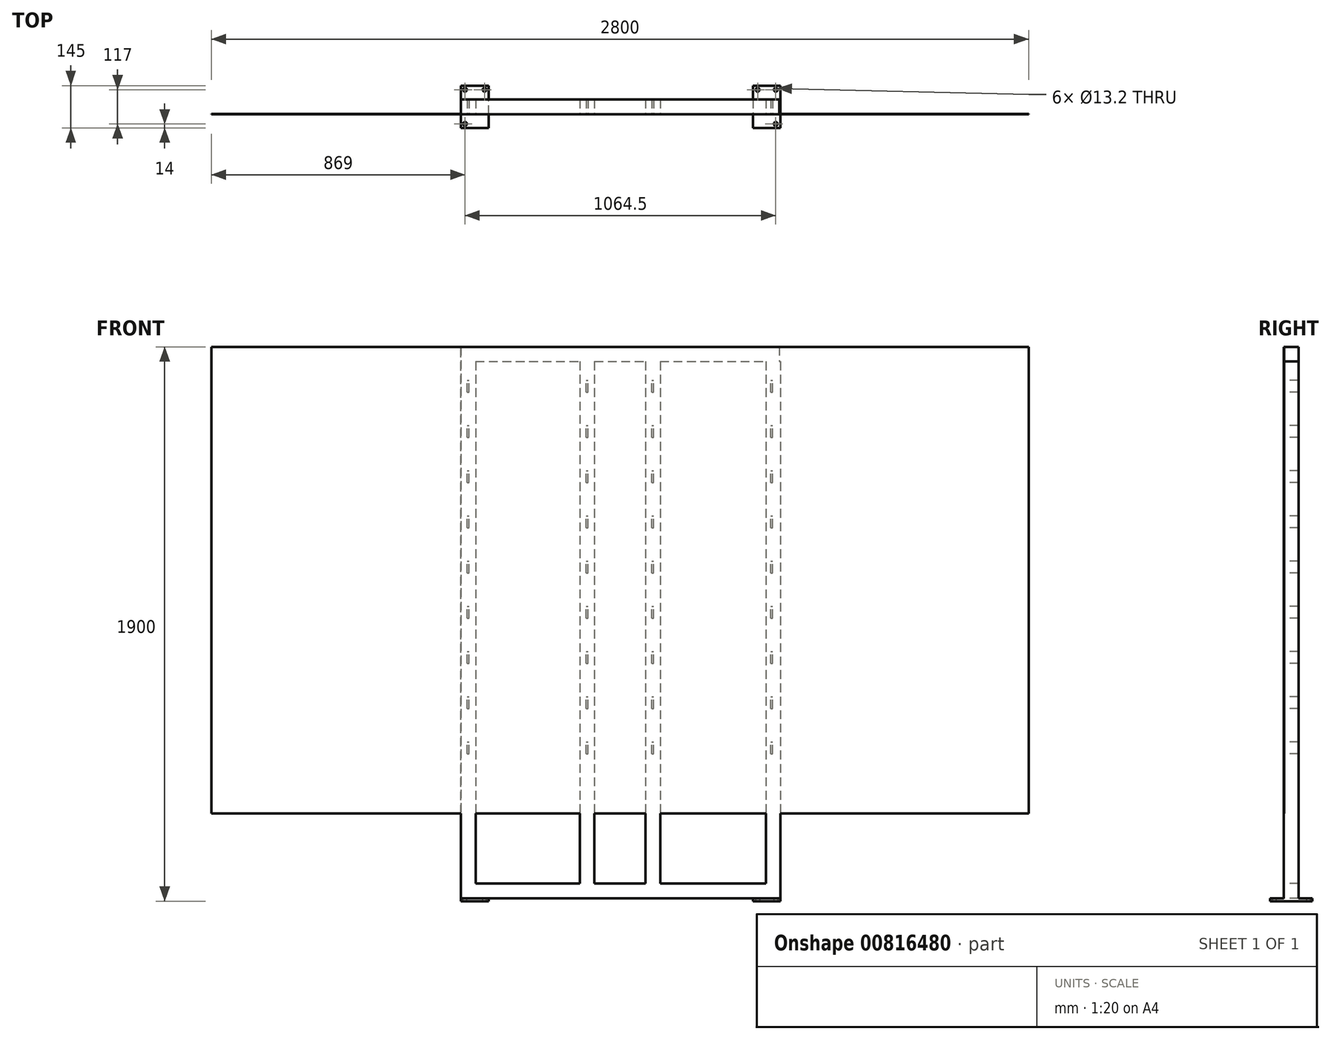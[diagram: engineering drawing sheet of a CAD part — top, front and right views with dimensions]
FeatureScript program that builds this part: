
annotation { "Feature Type Name" : "Feature", "Feature Type Description" : "" }
export const myFeature = defineFeature(function(context is Context, id is Id, definition is map)
    precondition{}
    {
        {
            var Q0;
            Q0=qCreatedBy(makeId("Top.planeOp"),FACE);
            var sketch = newSketch(context, id + "F0", { "sketchPlane" : qUnion([Q0])});
            skLineSegment(sketch, "E0.bottom", {"start": v(47.5, 72.5) * mm, "end": v(-47.5, 72.5) * mm});
            skLineSegment(sketch, "E0.top", {"start": v(47.5, -72.5) * mm, "end": v(-47.5, -72.5) * mm});
            skLineSegment(sketch, "E0.left", {"start": v(47.5, 72.5) * mm, "end": v(47.5, -72.5) * mm});
            skLineSegment(sketch, "E0.right", {"start": v(-47.5, 72.5) * mm, "end": v(-47.5, -72.5) * mm});
            skPoint(sketch, "E0.middle", {"position": v(0, 0) * mm});
            skSolve(sketch);
        }
        {
            var Q0;
            Q0=makeQuery(id+"F0.imprint","IMPRINT",FACE,{"disambiguationData":[TD([[makeQuery(id+"F0.imprint","IMPRINT",EDGE,{"derivedFrom":sQuery(id+"F0.wireOp",EDGE,"E0.bottom")}),1.0]])]});
            extrude(context, id + "F1", {"entities" : qUnion([Q0]), "depth" : 10 * mm, "offsetDistance" : 25 * mm});
        }
        {
            var Q0;
            Q0=qCreatedBy(makeId("Top.planeOp"),FACE);
            var sketch = newSketch(context, id + "F2", { "sketchPlane" : qUnion([Q0])});
            skPoint(sketch, "E1", {"position": v(31, 58.5) * mm});
            skPoint(sketch, "E2", {"position": v(31, -58.5) * mm});
            skPoint(sketch, "E3", {"position": v(-31, 58.5) * mm});
            skSolve(sketch);
        }
        {
            var Q0;
            Q0=sQuery(id+"F2.wireOp",VERTEX,"E1");
            var Q1;
            Q1=sQuery(id+"F2.wireOp",VERTEX,"E2");
            var Q2;
            Q2=sQuery(id+"F2.wireOp",VERTEX,"E3");
            var Q3;
            Q3=makeQuery(id+"F1.opExtrude","SWEPT_BODY",BODY,{"disambiguationData":[OSD([sQuery(id+"F0.wireOp",EDGE,"E0.bottom"),sQuery(id+"F0.wireOp",EDGE,"E0.top"),sQuery(id+"F0.wireOp",EDGE,"E0.left"),sQuery(id+"F0.wireOp",EDGE,"E0.right")])]});
            hole(context, id + "F3", {"style" : HoleStyle.SIMPLE, "endStyle" : HoleEndStyle.THROUGH, "oppositeDirection" : true, "standardTappedOrClearance" : lookupTablePath({ "standard" : "ISO", "fit" : "Normal", "size" : "M12", "type" : "Clearance" }), "standardBlindInLast" : lookupTablePath({ "fit" : "Standard", "standard" : "ISO", "size" : "M12", "type" : "Clearance" }), "holeDiameter" : 13.2 * mm, "majorDiameter" : 5 * mm, "isTappedThrough" : true, "tappedDepth" : 12 * mm, "tapClearance" : 3, "locations" : qUnion([Q0, Q1, Q2]), "scope" : qUnion([Q3])});
        }
        {
            var Q0;
            Q0=makeQuery(id+"F1.opExtrude","CAP_FACE",FACE,{"disambiguationData":[OSD([sQuery(id+"F0.wireOp",EDGE,"E0.bottom"),sQuery(id+"F0.wireOp",EDGE,"E0.top"),sQuery(id+"F0.wireOp",EDGE,"E0.left"),sQuery(id+"F0.wireOp",EDGE,"E0.right")])],"isStart":false});
            var sketch = newSketch(context, id + "F4", { "sketchPlane" : qUnion([Q0])});
            skLineSegment(sketch, "E4.bottom", {"start": v(47.5, 25) * mm, "end": v(-47.5, 25) * mm});
            skLineSegment(sketch, "E4.top", {"start": v(47.5, -25) * mm, "end": v(-47.5, -25) * mm});
            skLineSegment(sketch, "E4.left", {"start": v(47.5, 25) * mm, "end": v(47.5, -25) * mm});
            skLineSegment(sketch, "E4.right", {"start": v(-47.5, 25) * mm, "end": v(-47.5, -25) * mm});
            skPoint(sketch, "E4.middle", {"position": v(0, 0) * mm});
            skSolve(sketch);
        }
        {
            var Q0;
            Q0=qSketchRegion(id+"F4",true);
            extrude(context, id + "F5", {"entities" : qUnion([Q0]), "operationType" : NewBodyOperationType.ADD, "depth" : 50 * mm, "offsetDistance" : 25 * mm});
        }
        {
            var Q0;
            Q0=makeQuery(id+"F5.boolean.opBoolean","MERGE",FACE,{"derivedFrom":[makeQuery(id+"F1.opExtrude","SWEPT_FACE",FACE,{"disambiguationData":[OSD([sQuery(id+"F0.wireOp",EDGE,"E0.right")])]}),makeQuery(id+"F5.opExtrude","SWEPT_FACE",FACE,{"disambiguationData":[OSD([sQuery(id+"F4.wireOp",EDGE,"E4.right")])]})]});
            var sketch = newSketch(context, id + "F6", { "sketchPlane" : qUnion([Q0])});
            skLineSegment(sketch, "E5.bottom", {"start": v(-25, 60) * mm, "end": v(25, 60) * mm});
            skLineSegment(sketch, "E5.top", {"start": v(-25, 10) * mm, "end": v(25, 10) * mm});
            skLineSegment(sketch, "E5.left", {"start": v(-25, 60) * mm, "end": v(-25, 10) * mm});
            skLineSegment(sketch, "E5.right", {"start": v(25, 60) * mm, "end": v(25, 10) * mm});
            skSolve(sketch);
        }
        {
            var Q0;
            Q0=qSketchRegion(id+"F6",true);
            extrude(context, id + "F7", {"entities" : qUnion([Q0]), "operationType" : NewBodyOperationType.ADD, "depth" : 1000 * mm, "offsetDistance" : 25 * mm});
        }
        {
            var Q0;
            Q0=makeQuery(id+"F7.opExtrude","SWEPT_FACE",FACE,{"disambiguationData":[OSD([sQuery(id+"F6.wireOp",EDGE,"E5.top")])]});
            var sketch = newSketch(context, id + "F8", { "sketchPlane" : qUnion([Q0])});
            skLineSegment(sketch, "E6.bottom", {"start": v(-952.5, 72.5) * mm, "end": v(-1047.5, 72.5) * mm});
            skLineSegment(sketch, "E6.top", {"start": v(-952.5, -72.5) * mm, "end": v(-1047.5, -72.5) * mm});
            skLineSegment(sketch, "E6.left", {"start": v(-952.5, 72.5) * mm, "end": v(-952.5, -72.5) * mm});
            skLineSegment(sketch, "E6.right", {"start": v(-1047.5, 72.5) * mm, "end": v(-1047.5, -72.5) * mm});
            skPoint(sketch, "E6.middle", {"position": v(-1000, 0) * mm});
            skPoint(sketch, "E6.middle.positionSnap0", {"position": v(-1047.5, 0) * mm});
            skPoint(sketch, "E6.centerSnap0", {"position": v(-1047.5, 0) * mm});
            skSolve(sketch);
        }
        {
            var Q0;
            Q0=qSketchRegion(id+"F8",true);
            extrude(context, id + "F9", {"entities" : qUnion([Q0]), "operationType" : NewBodyOperationType.ADD, "depth" : 10 * mm, "offsetDistance" : 25 * mm});
        }
        {
            var Q0;
            {var subQ2=sQuery(id+"F8.wireOp",EDGE,"E6.top");var subQ3=sQuery(id+"F8.wireOp",EDGE,"E6.left");var subQ4=sQuery(id+"F8.wireOp",EDGE,"E6.right");Q0=makeQuery(id+"F9.boolean.opBoolean","SPLIT",FACE,{"disambiguationData":[TD([makeQuery(id+"F5.opExtrude","SWEPT_FACE",FACE,{"disambiguationData":[OSD([sQuery(id+"F4.wireOp",EDGE,"E4.bottom")])]})])],"derivedFrom":makeQuery(id+"F9.opExtrude","CAP_FACE",FACE,{"disambiguationData":[OSD([sQuery(id+"F8.wireOp",EDGE,"E6.bottom"),subQ2,subQ3,subQ4])],"isStart":true})});}
            var sketch = newSketch(context, id + "F10", { "sketchPlane" : qUnion([Q0])});
            skPoint(sketch, "E7", {"position": v(-1033.5, 58.5) * mm});
            skPoint(sketch, "E8", {"position": v(-966.5, 58.5) * mm});
            skPoint(sketch, "E9", {"position": v(-1033.5, -58.5) * mm});
            skSolve(sketch);
        }
        {
            var Q0;
            Q0=sQuery(id+"F10.wireOp",VERTEX,"E8");
            var Q1;
            Q1=sQuery(id+"F10.wireOp",VERTEX,"E9");
            var Q2;
            Q2=sQuery(id+"F10.wireOp",VERTEX,"E7");
            var Q3;
            Q3=makeQuery(id+"F1.opExtrude","SWEPT_BODY",BODY,{"disambiguationData":[OSD([sQuery(id+"F0.wireOp",EDGE,"E0.bottom"),sQuery(id+"F0.wireOp",EDGE,"E0.top"),sQuery(id+"F0.wireOp",EDGE,"E0.left"),sQuery(id+"F0.wireOp",EDGE,"E0.right")])]});
            hole(context, id + "F11", {"style" : HoleStyle.SIMPLE, "endStyle" : HoleEndStyle.THROUGH, "standardTappedOrClearance" : lookupTablePath({ "standard" : "ISO", "fit" : "Normal", "size" : "M12", "type" : "Clearance" }), "standardBlindInLast" : lookupTablePath({ "fit" : "Standard", "standard" : "ISO", "size" : "M12", "type" : "Clearance" }), "holeDiameter" : 13.2 * mm, "majorDiameter" : 5 * mm, "isTappedThrough" : true, "tappedDepth" : 12 * mm, "tapClearance" : 3, "locations" : qUnion([Q0, Q1, Q2]), "scope" : qUnion([Q3])});
        }
        {
            var Q0;
            Q0=makeQuery(id+"F7.boolean.opBoolean","MERGE",FACE,{"derivedFrom":[makeQuery(id+"F5.opExtrude","CAP_FACE",FACE,{"disambiguationData":[OSD([sQuery(id+"F4.wireOp",EDGE,"E4.bottom"),sQuery(id+"F4.wireOp",EDGE,"E4.top"),sQuery(id+"F4.wireOp",EDGE,"E4.left"),sQuery(id+"F4.wireOp",EDGE,"E4.right")])],"isStart":false}),makeQuery(id+"F7.opExtrude","SWEPT_FACE",FACE,{"disambiguationData":[OSD([sQuery(id+"F6.wireOp",EDGE,"E5.bottom")])]})]});
            var sketch = newSketch(context, id + "F12", { "sketchPlane" : qUnion([Q0])});
            skLineSegment(sketch, "E10.bottom", {"start": v(47.5, 25) * mm, "end": v(-2.5, 25) * mm});
            skLineSegment(sketch, "E10.top", {"start": v(47.5, -25) * mm, "end": v(-2.5, -25) * mm});
            skLineSegment(sketch, "E10.left", {"start": v(-2.5, 25) * mm, "end": v(-2.5, -25) * mm});
            skLineSegment(sketch, "E10.right", {"start": v(47.5, 25) * mm, "end": v(47.5, -25) * mm});
            skPoint(sketch, "E10.middle", {"position": v(22.5, 0) * mm});
            skPoint(sketch, "E10.middle.positionSnap0", {"position": v(47.5, 0) * mm});
            skPoint(sketch, "E10.centerSnap0", {"position": v(47.5, 0) * mm});
            skLineSegment(sketch, "E11.bottom", {"start": v(-365, 25) * mm, "end": v(-415, 25) * mm});
            skLineSegment(sketch, "E11.top", {"start": v(-365, -25) * mm, "end": v(-415, -25) * mm});
            skLineSegment(sketch, "E11.left", {"start": v(-365, 25) * mm, "end": v(-365, -25) * mm});
            skLineSegment(sketch, "E11.right", {"start": v(-415, 25) * mm, "end": v(-415, -25) * mm});
            skPoint(sketch, "E11.middle", {"position": v(-390, 0) * mm});
            skLineSegment(sketch, "E12.bottom", {"start": v(-997.5, 25) * mm, "end": v(-1047.5, 25) * mm});
            skLineSegment(sketch, "E12.top", {"start": v(-997.5, -25) * mm, "end": v(-1047.5, -25) * mm});
            skLineSegment(sketch, "E12.left", {"start": v(-997.5, 25) * mm, "end": v(-997.5, -25) * mm});
            skLineSegment(sketch, "E12.right", {"start": v(-1047.5, 25) * mm, "end": v(-1047.5, -25) * mm});
            skPoint(sketch, "E12.middle", {"position": v(-1022.5, 0) * mm});
            skLineSegment(sketch, "E13.bottom", {"start": v(-590, 25) * mm, "end": v(-640, 25) * mm});
            skLineSegment(sketch, "E13.top", {"start": v(-590, -25) * mm, "end": v(-640, -25) * mm});
            skLineSegment(sketch, "E13.left", {"start": v(-590, 25) * mm, "end": v(-590, -25) * mm});
            skLineSegment(sketch, "E13.right", {"start": v(-640, 25) * mm, "end": v(-640, -25) * mm});
            skPoint(sketch, "E13.middle", {"position": v(-615, 0) * mm});
            skSolve(sketch);
        }
        {
            var Q0;
            Q0 = qSketchRegion(id + "F12", true);
            extrude(context, id + "F13", {"entities" : qUnion([Q0]), "operationType" : NewBodyOperationType.ADD, "depth" : 1790 * mm, "offsetDistance" : 25 * mm});
        }
        {
            var Q0;
            Q0=makeQuery(id+"F13.opExtrude","CAP_FACE",FACE,{"disambiguationData":[OSD([sQuery(id+"F12.wireOp",EDGE,"E12.bottom"),sQuery(id+"F12.wireOp",EDGE,"E12.top"),sQuery(id+"F12.wireOp",EDGE,"E12.left"),sQuery(id+"F12.wireOp",EDGE,"E12.right")])],"isStart":false});
            var sketch = newSketch(context, id + "F14", { "sketchPlane" : qUnion([Q0])});
            skLineSegment(sketch, "E14.bottom", {"start": v(-1047.5, 25) * mm, "end": v(-1047.5, 25) * mm});
            skLineSegment(sketch, "E14.top", {"start": v(-1047.5, -25) * mm, "end": v(-1047.5, -25) * mm});
            skLineSegment(sketch, "E14.left", {"start": v(-1047.5, 25) * mm, "end": v(-1047.5, -25) * mm});
            skLineSegment(sketch, "E14.right", {"start": v(-1047.5, 25) * mm, "end": v(-1047.5, -25) * mm});
            skLineSegment(sketch, "E15.bottom", {"start": v(-1047.5, 25) * mm, "end": v(42.99, 25) * mm});
            skLineSegment(sketch, "E15.top", {"start": v(-1047.5, -25) * mm, "end": v(42.99, -25) * mm});
            skLineSegment(sketch, "E15.right", {"start": v(42.99, 25) * mm, "end": v(42.99, -25) * mm});
            skSolve(sketch);
        }
        {
            var Q0;
            Q0 = qSketchRegion(id + "F14", true);
            extrude(context, id + "F15", {"entities" : qUnion([Q0]), "operationType" : NewBodyOperationType.ADD, "depth" : 50 * mm, "offsetDistance" : 25 * mm});
        }
        {
            var Q0;
            Q0=makeQuery(id+"F15.boolean.opBoolean","MERGE",FACE,{"derivedFrom":[makeQuery(id+"F13.boolean.opBoolean","MERGE",FACE,{"derivedFrom":[makeQuery(id+"F7.boolean.opBoolean","MERGE",FACE,{"derivedFrom":[makeQuery(id+"F5.opExtrude","SWEPT_FACE",FACE,{"disambiguationData":[OSD([sQuery(id+"F4.wireOp",EDGE,"E4.top")])]}),makeQuery(id+"F7.opExtrude","SWEPT_FACE",FACE,{"disambiguationData":[OSD([sQuery(id+"F6.wireOp",EDGE,"E5.right")])]})]}),makeQuery(id+"F13.opExtrude","SWEPT_FACE",FACE,{"disambiguationData":[OSD([sQuery(id+"F12.wireOp",EDGE,"E10.top")])]}),makeQuery(id+"F13.opExtrude","SWEPT_FACE",FACE,{"disambiguationData":[OSD([sQuery(id+"F12.wireOp",EDGE,"E11.top")])]}),makeQuery(id+"F13.opExtrude","SWEPT_FACE",FACE,{"disambiguationData":[OSD([sQuery(id+"F12.wireOp",EDGE,"E12.top")])]}),makeQuery(id+"F13.opExtrude","SWEPT_FACE",FACE,{"disambiguationData":[OSD([sQuery(id+"F12.wireOp",EDGE,"E13.top")])]})]}),makeQuery(id+"F15.opExtrude","SWEPT_FACE",FACE,{"disambiguationData":[OSD([sQuery(id+"F14.wireOp",EDGE,"E15.top")])]})]});
            var sketch = newSketch(context, id + "F16", { "sketchPlane" : qUnion([Q0])});
            skLineSegment(sketch, "E16.bottom", {"start": v(-1019.5, 545) * mm, "end": v(-1025.5, 545) * mm});
            skLineSegment(sketch, "E16.top", {"start": v(-1019.5, 505) * mm, "end": v(-1025.5, 505) * mm});
            skLineSegment(sketch, "E16.left", {"start": v(-1019.5, 545) * mm, "end": v(-1019.5, 505) * mm});
            skLineSegment(sketch, "E16.right", {"start": v(-1025.5, 545) * mm, "end": v(-1025.5, 505) * mm});
            skPoint(sketch, "E16.middle", {"position": v(-1022.5, 525) * mm});
            skLineSegment(sketch, "E17.0.1.0", {"start": v(-1025.5, 700) * mm, "end": v(-1025.5, 660) * mm});
            skLineSegment(sketch, "E17.0.1.1", {"start": v(-1019.5, 700) * mm, "end": v(-1025.5, 700) * mm});
            skLineSegment(sketch, "E17.0.1.2", {"start": v(-1019.5, 700) * mm, "end": v(-1019.5, 660) * mm});
            skLineSegment(sketch, "E17.0.1.3", {"start": v(-1019.5, 660) * mm, "end": v(-1025.5, 660) * mm});
            skLineSegment(sketch, "E17.0.2.0", {"start": v(-1025.5, 855) * mm, "end": v(-1025.5, 815) * mm});
            skLineSegment(sketch, "E17.0.2.1", {"start": v(-1019.5, 855) * mm, "end": v(-1025.5, 855) * mm});
            skLineSegment(sketch, "E17.0.2.2", {"start": v(-1019.5, 855) * mm, "end": v(-1019.5, 815) * mm});
            skLineSegment(sketch, "E17.0.2.3", {"start": v(-1019.5, 815) * mm, "end": v(-1025.5, 815) * mm});
            skLineSegment(sketch, "E17.0.3.0", {"start": v(-1025.5, 1010) * mm, "end": v(-1025.5, 970) * mm});
            skLineSegment(sketch, "E17.0.3.1", {"start": v(-1019.5, 1010) * mm, "end": v(-1025.5, 1010) * mm});
            skLineSegment(sketch, "E17.0.3.2", {"start": v(-1019.5, 1010) * mm, "end": v(-1019.5, 970) * mm});
            skLineSegment(sketch, "E17.0.3.3", {"start": v(-1019.5, 970) * mm, "end": v(-1025.5, 970) * mm});
            skLineSegment(sketch, "E17.0.4.0", {"start": v(-1025.5, 1165) * mm, "end": v(-1025.5, 1125) * mm});
            skLineSegment(sketch, "E17.0.4.1", {"start": v(-1019.5, 1165) * mm, "end": v(-1025.5, 1165) * mm});
            skLineSegment(sketch, "E17.0.4.2", {"start": v(-1019.5, 1165) * mm, "end": v(-1019.5, 1125) * mm});
            skLineSegment(sketch, "E17.0.4.3", {"start": v(-1019.5, 1125) * mm, "end": v(-1025.5, 1125) * mm});
            skLineSegment(sketch, "E17.0.5.0", {"start": v(-1025.5, 1320) * mm, "end": v(-1025.5, 1280) * mm});
            skLineSegment(sketch, "E17.0.5.1", {"start": v(-1019.5, 1320) * mm, "end": v(-1025.5, 1320) * mm});
            skLineSegment(sketch, "E17.0.5.2", {"start": v(-1019.5, 1320) * mm, "end": v(-1019.5, 1280) * mm});
            skLineSegment(sketch, "E17.0.5.3", {"start": v(-1019.5, 1280) * mm, "end": v(-1025.5, 1280) * mm});
            skLineSegment(sketch, "E17.0.6.0", {"start": v(-1025.5, 1475) * mm, "end": v(-1025.5, 1435) * mm});
            skLineSegment(sketch, "E17.0.6.1", {"start": v(-1019.5, 1475) * mm, "end": v(-1025.5, 1475) * mm});
            skLineSegment(sketch, "E17.0.6.2", {"start": v(-1019.5, 1475) * mm, "end": v(-1019.5, 1435) * mm});
            skLineSegment(sketch, "E17.0.6.3", {"start": v(-1019.5, 1435) * mm, "end": v(-1025.5, 1435) * mm});
            skLineSegment(sketch, "E17.0.7.0", {"start": v(-1025.5, 1630) * mm, "end": v(-1025.5, 1590) * mm});
            skLineSegment(sketch, "E17.0.7.1", {"start": v(-1019.5, 1630) * mm, "end": v(-1025.5, 1630) * mm});
            skLineSegment(sketch, "E17.0.7.2", {"start": v(-1019.5, 1630) * mm, "end": v(-1019.5, 1590) * mm});
            skLineSegment(sketch, "E17.0.7.3", {"start": v(-1019.5, 1590) * mm, "end": v(-1025.5, 1590) * mm});
            skLineSegment(sketch, "E17.0.8.0", {"start": v(-1025.5, 1785) * mm, "end": v(-1025.5, 1745) * mm});
            skLineSegment(sketch, "E17.0.8.1", {"start": v(-1019.5, 1785) * mm, "end": v(-1025.5, 1785) * mm});
            skLineSegment(sketch, "E17.0.8.2", {"start": v(-1019.5, 1785) * mm, "end": v(-1019.5, 1745) * mm});
            skLineSegment(sketch, "E17.0.8.3", {"start": v(-1019.5, 1745) * mm, "end": v(-1025.5, 1745) * mm});
            skLineSegment(sketch, "E17.1.0.0", {"start": v(-618, 545) * mm, "end": v(-618, 505) * mm});
            skLineSegment(sketch, "E17.1.0.1", {"start": v(-612, 545) * mm, "end": v(-618, 545) * mm});
            skLineSegment(sketch, "E17.1.0.2", {"start": v(-612, 545) * mm, "end": v(-612, 505) * mm});
            skLineSegment(sketch, "E17.1.0.3", {"start": v(-612, 505) * mm, "end": v(-618, 505) * mm});
            skLineSegment(sketch, "E17.1.1.0", {"start": v(-618, 700) * mm, "end": v(-618, 660) * mm});
            skLineSegment(sketch, "E17.1.1.1", {"start": v(-612, 700) * mm, "end": v(-618, 700) * mm});
            skLineSegment(sketch, "E17.1.1.2", {"start": v(-612, 700) * mm, "end": v(-612, 660) * mm});
            skLineSegment(sketch, "E17.1.1.3", {"start": v(-612, 660) * mm, "end": v(-618, 660) * mm});
            skLineSegment(sketch, "E17.1.2.0", {"start": v(-618, 855) * mm, "end": v(-618, 815) * mm});
            skLineSegment(sketch, "E17.1.2.1", {"start": v(-612, 855) * mm, "end": v(-618, 855) * mm});
            skLineSegment(sketch, "E17.1.2.2", {"start": v(-612, 855) * mm, "end": v(-612, 815) * mm});
            skLineSegment(sketch, "E17.1.2.3", {"start": v(-612, 815) * mm, "end": v(-618, 815) * mm});
            skLineSegment(sketch, "E17.1.3.0", {"start": v(-618, 1010) * mm, "end": v(-618, 970) * mm});
            skLineSegment(sketch, "E17.1.3.1", {"start": v(-612, 1010) * mm, "end": v(-618, 1010) * mm});
            skLineSegment(sketch, "E17.1.3.2", {"start": v(-612, 1010) * mm, "end": v(-612, 970) * mm});
            skLineSegment(sketch, "E17.1.3.3", {"start": v(-612, 970) * mm, "end": v(-618, 970) * mm});
            skLineSegment(sketch, "E17.1.4.0", {"start": v(-618, 1165) * mm, "end": v(-618, 1125) * mm});
            skLineSegment(sketch, "E17.1.4.1", {"start": v(-612, 1165) * mm, "end": v(-618, 1165) * mm});
            skLineSegment(sketch, "E17.1.4.2", {"start": v(-612, 1165) * mm, "end": v(-612, 1125) * mm});
            skLineSegment(sketch, "E17.1.4.3", {"start": v(-612, 1125) * mm, "end": v(-618, 1125) * mm});
            skLineSegment(sketch, "E17.1.5.0", {"start": v(-618, 1320) * mm, "end": v(-618, 1280) * mm});
            skLineSegment(sketch, "E17.1.5.1", {"start": v(-612, 1320) * mm, "end": v(-618, 1320) * mm});
            skLineSegment(sketch, "E17.1.5.2", {"start": v(-612, 1320) * mm, "end": v(-612, 1280) * mm});
            skLineSegment(sketch, "E17.1.5.3", {"start": v(-612, 1280) * mm, "end": v(-618, 1280) * mm});
            skLineSegment(sketch, "E17.1.6.0", {"start": v(-618, 1475) * mm, "end": v(-618, 1435) * mm});
            skLineSegment(sketch, "E17.1.6.1", {"start": v(-612, 1475) * mm, "end": v(-618, 1475) * mm});
            skLineSegment(sketch, "E17.1.6.2", {"start": v(-612, 1475) * mm, "end": v(-612, 1435) * mm});
            skLineSegment(sketch, "E17.1.6.3", {"start": v(-612, 1435) * mm, "end": v(-618, 1435) * mm});
            skLineSegment(sketch, "E17.1.7.0", {"start": v(-618, 1630) * mm, "end": v(-618, 1590) * mm});
            skLineSegment(sketch, "E17.1.7.1", {"start": v(-612, 1630) * mm, "end": v(-618, 1630) * mm});
            skLineSegment(sketch, "E17.1.7.2", {"start": v(-612, 1630) * mm, "end": v(-612, 1590) * mm});
            skLineSegment(sketch, "E17.1.7.3", {"start": v(-612, 1590) * mm, "end": v(-618, 1590) * mm});
            skLineSegment(sketch, "E17.1.8.0", {"start": v(-618, 1785) * mm, "end": v(-618, 1745) * mm});
            skLineSegment(sketch, "E17.1.8.1", {"start": v(-612, 1785) * mm, "end": v(-618, 1785) * mm});
            skLineSegment(sketch, "E17.1.8.2", {"start": v(-612, 1785) * mm, "end": v(-612, 1745) * mm});
            skLineSegment(sketch, "E17.1.8.3", {"start": v(-612, 1745) * mm, "end": v(-618, 1745) * mm});
            skLineSegment(sketch, "E17.direction1", {"start": v(-1025.5, 505) * mm, "end": v(-618, 505) * mm, "construction": true});
            skLineSegment(sketch, "E17.direction2", {"start": v(-1025.5, 505) * mm, "end": v(-1025.5, 660) * mm, "construction": true});
            skSolve(sketch);
        }
        {
            var Q0;
            Q0 = qSketchRegion(id + "F16", true);
            extrude(context, id + "F17", {"entities" : qUnion([Q0]), "operationType" : NewBodyOperationType.REMOVE, "endBound" : BoundingType.THROUGH_ALL, "oppositeDirection" : true, "depth" : 25 * mm, "offsetDistance" : 25 * mm});
        }
        {
            var Q0;
            Q0=makeQuery(id+"F15.boolean.opBoolean","MERGE",FACE,{"derivedFrom":[makeQuery(id+"F13.boolean.opBoolean","MERGE",FACE,{"derivedFrom":[makeQuery(id+"F7.boolean.opBoolean","MERGE",FACE,{"derivedFrom":[makeQuery(id+"F5.opExtrude","SWEPT_FACE",FACE,{"disambiguationData":[OSD([sQuery(id+"F4.wireOp",EDGE,"E4.top")])]}),makeQuery(id+"F7.opExtrude","SWEPT_FACE",FACE,{"disambiguationData":[OSD([sQuery(id+"F6.wireOp",EDGE,"E5.right")])]})]}),makeQuery(id+"F13.opExtrude","SWEPT_FACE",FACE,{"disambiguationData":[OSD([sQuery(id+"F12.wireOp",EDGE,"E10.top")])]}),makeQuery(id+"F13.opExtrude","SWEPT_FACE",FACE,{"disambiguationData":[OSD([sQuery(id+"F12.wireOp",EDGE,"E11.top")])]}),makeQuery(id+"F13.opExtrude","SWEPT_FACE",FACE,{"disambiguationData":[OSD([sQuery(id+"F12.wireOp",EDGE,"E12.top")])]}),makeQuery(id+"F13.opExtrude","SWEPT_FACE",FACE,{"disambiguationData":[OSD([sQuery(id+"F12.wireOp",EDGE,"E13.top")])]})]}),makeQuery(id+"F15.opExtrude","SWEPT_FACE",FACE,{"disambiguationData":[OSD([sQuery(id+"F14.wireOp",EDGE,"E15.top")])]})]});
            var sketch = newSketch(context, id + "F18", { "sketchPlane" : qUnion([Q0])});
            skLineSegment(sketch, "E18.bottom", {"start": v(-387, 545) * mm, "end": v(-393, 545) * mm});
            skLineSegment(sketch, "E18.top", {"start": v(-387, 505) * mm, "end": v(-393, 505) * mm});
            skLineSegment(sketch, "E18.left", {"start": v(-387, 545) * mm, "end": v(-387, 505) * mm});
            skLineSegment(sketch, "E18.right", {"start": v(-393, 545) * mm, "end": v(-393, 505) * mm});
            skPoint(sketch, "E18.middle", {"position": v(-390, 525) * mm});
            skPoint(sketch, "E18.middle.positionSnap0", {"position": v(-618, 525) * mm});
            skPoint(sketch, "E18.centerSnap0", {"position": v(-618, 525) * mm});
            skLineSegment(sketch, "E19.0.1.0", {"start": v(-393, 700) * mm, "end": v(-393, 660) * mm});
            skLineSegment(sketch, "E19.0.1.1", {"start": v(-387, 700) * mm, "end": v(-393, 700) * mm});
            skLineSegment(sketch, "E19.0.1.2", {"start": v(-387, 700) * mm, "end": v(-387, 660) * mm});
            skLineSegment(sketch, "E19.0.1.3", {"start": v(-387, 660) * mm, "end": v(-393, 660) * mm});
            skLineSegment(sketch, "E19.0.2.0", {"start": v(-393, 855) * mm, "end": v(-393, 815) * mm});
            skLineSegment(sketch, "E19.0.2.1", {"start": v(-387, 855) * mm, "end": v(-393, 855) * mm});
            skLineSegment(sketch, "E19.0.2.2", {"start": v(-387, 855) * mm, "end": v(-387, 815) * mm});
            skLineSegment(sketch, "E19.0.2.3", {"start": v(-387, 815) * mm, "end": v(-393, 815) * mm});
            skLineSegment(sketch, "E19.0.3.0", {"start": v(-393, 1010) * mm, "end": v(-393, 970) * mm});
            skLineSegment(sketch, "E19.0.3.1", {"start": v(-387, 1010) * mm, "end": v(-393, 1010) * mm});
            skLineSegment(sketch, "E19.0.3.2", {"start": v(-387, 1010) * mm, "end": v(-387, 970) * mm});
            skLineSegment(sketch, "E19.0.3.3", {"start": v(-387, 970) * mm, "end": v(-393, 970) * mm});
            skLineSegment(sketch, "E19.0.4.0", {"start": v(-393, 1165) * mm, "end": v(-393, 1125) * mm});
            skLineSegment(sketch, "E19.0.4.1", {"start": v(-387, 1165) * mm, "end": v(-393, 1165) * mm});
            skLineSegment(sketch, "E19.0.4.2", {"start": v(-387, 1165) * mm, "end": v(-387, 1125) * mm});
            skLineSegment(sketch, "E19.0.4.3", {"start": v(-387, 1125) * mm, "end": v(-393, 1125) * mm});
            skLineSegment(sketch, "E19.0.5.0", {"start": v(-393, 1320) * mm, "end": v(-393, 1280) * mm});
            skLineSegment(sketch, "E19.0.5.1", {"start": v(-387, 1320) * mm, "end": v(-393, 1320) * mm});
            skLineSegment(sketch, "E19.0.5.2", {"start": v(-387, 1320) * mm, "end": v(-387, 1280) * mm});
            skLineSegment(sketch, "E19.0.5.3", {"start": v(-387, 1280) * mm, "end": v(-393, 1280) * mm});
            skLineSegment(sketch, "E19.0.6.0", {"start": v(-393, 1475) * mm, "end": v(-393, 1435) * mm});
            skLineSegment(sketch, "E19.0.6.1", {"start": v(-387, 1475) * mm, "end": v(-393, 1475) * mm});
            skLineSegment(sketch, "E19.0.6.2", {"start": v(-387, 1475) * mm, "end": v(-387, 1435) * mm});
            skLineSegment(sketch, "E19.0.6.3", {"start": v(-387, 1435) * mm, "end": v(-393, 1435) * mm});
            skLineSegment(sketch, "E19.0.7.0", {"start": v(-393, 1630) * mm, "end": v(-393, 1590) * mm});
            skLineSegment(sketch, "E19.0.7.1", {"start": v(-387, 1630) * mm, "end": v(-393, 1630) * mm});
            skLineSegment(sketch, "E19.0.7.2", {"start": v(-387, 1630) * mm, "end": v(-387, 1590) * mm});
            skLineSegment(sketch, "E19.0.7.3", {"start": v(-387, 1590) * mm, "end": v(-393, 1590) * mm});
            skLineSegment(sketch, "E19.0.8.0", {"start": v(-393, 1785) * mm, "end": v(-393, 1745) * mm});
            skLineSegment(sketch, "E19.0.8.1", {"start": v(-387, 1785) * mm, "end": v(-393, 1785) * mm});
            skLineSegment(sketch, "E19.0.8.2", {"start": v(-387, 1785) * mm, "end": v(-387, 1745) * mm});
            skLineSegment(sketch, "E19.0.8.3", {"start": v(-387, 1745) * mm, "end": v(-393, 1745) * mm});
            skLineSegment(sketch, "E19.1.0.0", {"start": v(14.5, 545) * mm, "end": v(14.5, 505) * mm});
            skLineSegment(sketch, "E19.1.0.1", {"start": v(20.5, 545) * mm, "end": v(14.5, 545) * mm});
            skLineSegment(sketch, "E19.1.0.2", {"start": v(20.5, 545) * mm, "end": v(20.5, 505) * mm});
            skLineSegment(sketch, "E19.1.0.3", {"start": v(20.5, 505) * mm, "end": v(14.5, 505) * mm});
            skLineSegment(sketch, "E19.1.1.0", {"start": v(14.5, 700) * mm, "end": v(14.5, 660) * mm});
            skLineSegment(sketch, "E19.1.1.1", {"start": v(20.5, 700) * mm, "end": v(14.5, 700) * mm});
            skLineSegment(sketch, "E19.1.1.2", {"start": v(20.5, 700) * mm, "end": v(20.5, 660) * mm});
            skLineSegment(sketch, "E19.1.1.3", {"start": v(20.5, 660) * mm, "end": v(14.5, 660) * mm});
            skLineSegment(sketch, "E19.1.2.0", {"start": v(14.5, 855) * mm, "end": v(14.5, 815) * mm});
            skLineSegment(sketch, "E19.1.2.1", {"start": v(20.5, 855) * mm, "end": v(14.5, 855) * mm});
            skLineSegment(sketch, "E19.1.2.2", {"start": v(20.5, 855) * mm, "end": v(20.5, 815) * mm});
            skLineSegment(sketch, "E19.1.2.3", {"start": v(20.5, 815) * mm, "end": v(14.5, 815) * mm});
            skLineSegment(sketch, "E19.1.3.0", {"start": v(14.5, 1010) * mm, "end": v(14.5, 970) * mm});
            skLineSegment(sketch, "E19.1.3.1", {"start": v(20.5, 1010) * mm, "end": v(14.5, 1010) * mm});
            skLineSegment(sketch, "E19.1.3.2", {"start": v(20.5, 1010) * mm, "end": v(20.5, 970) * mm});
            skLineSegment(sketch, "E19.1.3.3", {"start": v(20.5, 970) * mm, "end": v(14.5, 970) * mm});
            skLineSegment(sketch, "E19.1.4.0", {"start": v(14.5, 1165) * mm, "end": v(14.5, 1125) * mm});
            skLineSegment(sketch, "E19.1.4.1", {"start": v(20.5, 1165) * mm, "end": v(14.5, 1165) * mm});
            skLineSegment(sketch, "E19.1.4.2", {"start": v(20.5, 1165) * mm, "end": v(20.5, 1125) * mm});
            skLineSegment(sketch, "E19.1.4.3", {"start": v(20.5, 1125) * mm, "end": v(14.5, 1125) * mm});
            skLineSegment(sketch, "E19.1.5.0", {"start": v(14.5, 1320) * mm, "end": v(14.5, 1280) * mm});
            skLineSegment(sketch, "E19.1.5.1", {"start": v(20.5, 1320) * mm, "end": v(14.5, 1320) * mm});
            skLineSegment(sketch, "E19.1.5.2", {"start": v(20.5, 1320) * mm, "end": v(20.5, 1280) * mm});
            skLineSegment(sketch, "E19.1.5.3", {"start": v(20.5, 1280) * mm, "end": v(14.5, 1280) * mm});
            skLineSegment(sketch, "E19.1.6.0", {"start": v(14.5, 1475) * mm, "end": v(14.5, 1435) * mm});
            skLineSegment(sketch, "E19.1.6.1", {"start": v(20.5, 1475) * mm, "end": v(14.5, 1475) * mm});
            skLineSegment(sketch, "E19.1.6.2", {"start": v(20.5, 1475) * mm, "end": v(20.5, 1435) * mm});
            skLineSegment(sketch, "E19.1.6.3", {"start": v(20.5, 1435) * mm, "end": v(14.5, 1435) * mm});
            skLineSegment(sketch, "E19.1.7.0", {"start": v(14.5, 1630) * mm, "end": v(14.5, 1590) * mm});
            skLineSegment(sketch, "E19.1.7.1", {"start": v(20.5, 1630) * mm, "end": v(14.5, 1630) * mm});
            skLineSegment(sketch, "E19.1.7.2", {"start": v(20.5, 1630) * mm, "end": v(20.5, 1590) * mm});
            skLineSegment(sketch, "E19.1.7.3", {"start": v(20.5, 1590) * mm, "end": v(14.5, 1590) * mm});
            skLineSegment(sketch, "E19.1.8.0", {"start": v(14.5, 1785) * mm, "end": v(14.5, 1745) * mm});
            skLineSegment(sketch, "E19.1.8.1", {"start": v(20.5, 1785) * mm, "end": v(14.5, 1785) * mm});
            skLineSegment(sketch, "E19.1.8.2", {"start": v(20.5, 1785) * mm, "end": v(20.5, 1745) * mm});
            skLineSegment(sketch, "E19.1.8.3", {"start": v(20.5, 1745) * mm, "end": v(14.5, 1745) * mm});
            skLineSegment(sketch, "E19.direction1", {"start": v(-393, 505) * mm, "end": v(14.5, 505) * mm, "construction": true});
            skLineSegment(sketch, "E19.direction2", {"start": v(-393, 505) * mm, "end": v(-393, 660) * mm, "construction": true});
            skSolve(sketch);
        }
        {
            var Q0;
            Q0 = qSketchRegion(id + "F18", true);
            extrude(context, id + "F19", {"entities" : qUnion([Q0]), "operationType" : NewBodyOperationType.REMOVE, "endBound" : BoundingType.THROUGH_ALL, "oppositeDirection" : true, "depth" : 25 * mm, "offsetDistance" : 25 * mm});
        }
        {
            var Q0;
            Q0=makeQuery(id+"F15.boolean.opBoolean","MERGE",FACE,{"derivedFrom":[makeQuery(id+"F13.boolean.opBoolean","MERGE",FACE,{"derivedFrom":[makeQuery(id+"F7.boolean.opBoolean","MERGE",FACE,{"derivedFrom":[makeQuery(id+"F5.opExtrude","SWEPT_FACE",FACE,{"disambiguationData":[OSD([sQuery(id+"F4.wireOp",EDGE,"E4.top")])]}),makeQuery(id+"F7.opExtrude","SWEPT_FACE",FACE,{"disambiguationData":[OSD([sQuery(id+"F6.wireOp",EDGE,"E5.right")])]})]}),makeQuery(id+"F13.opExtrude","SWEPT_FACE",FACE,{"disambiguationData":[OSD([sQuery(id+"F12.wireOp",EDGE,"E10.top")])]}),makeQuery(id+"F13.opExtrude","SWEPT_FACE",FACE,{"disambiguationData":[OSD([sQuery(id+"F12.wireOp",EDGE,"E11.top")])]}),makeQuery(id+"F13.opExtrude","SWEPT_FACE",FACE,{"disambiguationData":[OSD([sQuery(id+"F12.wireOp",EDGE,"E12.top")])]}),makeQuery(id+"F13.opExtrude","SWEPT_FACE",FACE,{"disambiguationData":[OSD([sQuery(id+"F12.wireOp",EDGE,"E13.top")])]})]}),makeQuery(id+"F15.opExtrude","SWEPT_FACE",FACE,{"disambiguationData":[OSD([sQuery(id+"F14.wireOp",EDGE,"E15.top")])]})]});
            var sketch = newSketch(context, id + "F20", { "sketchPlane" : qUnion([Q0])});
            skLineSegment(sketch, "E20.bottom", {"start": v(-1902.5, 1900) * mm, "end": v(897.5, 1900) * mm});
            skLineSegment(sketch, "E20.top", {"start": v(-1902.5, 300) * mm, "end": v(897.5, 300) * mm});
            skLineSegment(sketch, "E20.left", {"start": v(-1902.5, 1900) * mm, "end": v(-1902.5, 300) * mm});
            skLineSegment(sketch, "E20.right", {"start": v(897.5, 1900) * mm, "end": v(897.5, 300) * mm});
            skSolve(sketch);
        }
        {
            var Q0;
            Q0 = qSketchRegion(id + "F20", true);
            extrude(context, id + "F21", {"entities" : qUnion([Q0]), "operationType" : NewBodyOperationType.ADD, "oppositeDirection" : true, "depth" : 1 * mm, "offsetDistance" : 25 * mm});
        }
    });
